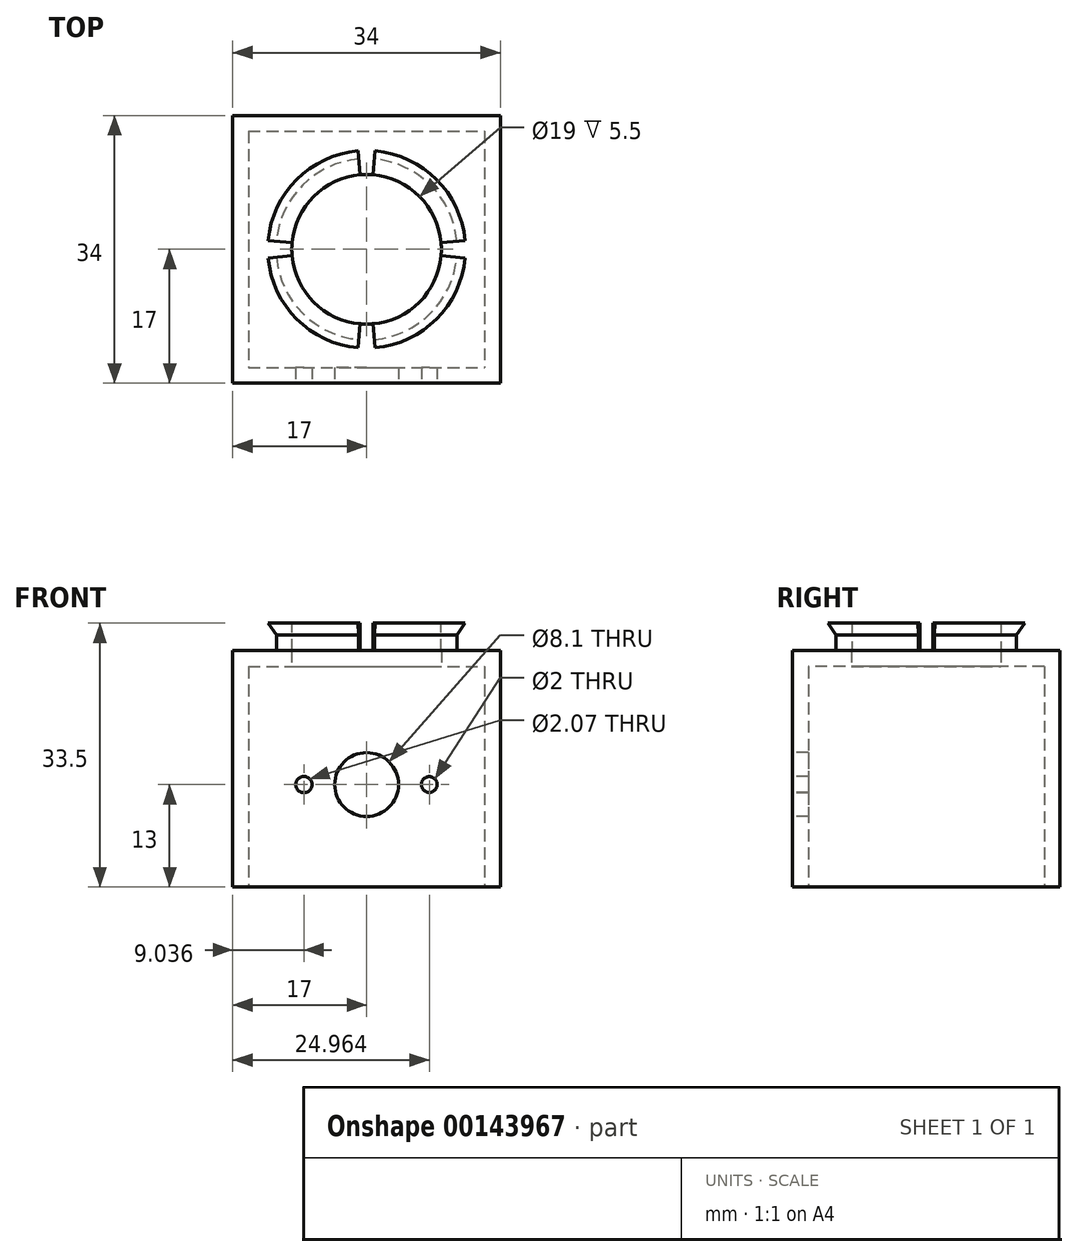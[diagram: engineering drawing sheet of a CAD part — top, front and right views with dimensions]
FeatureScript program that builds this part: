
annotation { "Feature Type Name" : "Feature", "Feature Type Description" : "" }
export const myFeature = defineFeature(function(context is Context, id is Id, definition is map)
    precondition{}
    {
        {
            var Q0;
            Q0=qCreatedBy(makeId("Top.planeOp"),FACE);
            var sketch = newSketch(context, id + "F0", { "sketchPlane" : qUnion([Q0])});
            skLineSegment(sketch, "E0.bottom", {"start": v(-15, 15) * mm, "end": v(15, 15) * mm});
            skLineSegment(sketch, "E0.top", {"start": v(-15, -15) * mm, "end": v(15, -15) * mm});
            skLineSegment(sketch, "E0.left", {"start": v(-15, 15) * mm, "end": v(-15, -15) * mm});
            skLineSegment(sketch, "E0.right", {"start": v(15, 15) * mm, "end": v(15, -15) * mm});
            skPoint(sketch, "E0.middle", {"position": v(0, 0) * mm});
            skLineSegment(sketch, "E1.bottom", {"start": v(0, 0) * mm, "end": v(0, 0) * mm});
            skLineSegment(sketch, "E1.top", {"start": v(0, 0) * mm, "end": v(0, 0) * mm});
            skLineSegment(sketch, "E1.left", {"start": v(0, 0) * mm, "end": v(0, 0) * mm});
            skLineSegment(sketch, "E1.right", {"start": v(0, 0) * mm, "end": v(0, 0) * mm});
            skLineSegment(sketch, "E2.bottom", {"start": v(-17, 17) * mm, "end": v(17, 17) * mm});
            skLineSegment(sketch, "E2.top", {"start": v(-17, -17) * mm, "end": v(17, -17) * mm});
            skLineSegment(sketch, "E2.left", {"start": v(-17, 17) * mm, "end": v(-17, -17) * mm});
            skLineSegment(sketch, "E2.right", {"start": v(17, 17) * mm, "end": v(17, -17) * mm});
            skSolve(sketch);
        }
        {
            var Q0;
            Q0=makeQuery(id+"F0.imprint","IMPRINT",FACE,{"disambiguationData":[TD([[makeQuery(id+"F0.imprint","IMPRINT",EDGE,{"derivedFrom":sQuery(id+"F0.wireOp",EDGE,"E0.bottom")}),1.0]])]});
            var Q1;
            Q1=makeQuery(id+"F0.imprint","IMPRINT",FACE,{"disambiguationData":[TD([[makeQuery(id+"F0.imprint","IMPRINT",EDGE,{"derivedFrom":sQuery(id+"F0.wireOp",EDGE,"E0.bottom")}),-1.0]])]});
            extrude(context, id + "F1", {"entities" : qUnion([Q0, Q1]), "oppositeDirection" : true, "depth" : 2 * mm});
        }
        {
            var Q0;
            Q0=makeQuery(id+"F0.imprint","IMPRINT",FACE,{"disambiguationData":[TD([[makeQuery(id+"F0.imprint","IMPRINT",EDGE,{"derivedFrom":sQuery(id+"F0.wireOp",EDGE,"E0.bottom")}),1.0]])]});
            extrude(context, id + "F2", {"entities" : qUnion([Q0]), "operationType" : NewBodyOperationType.ADD, "depth" : 28 * mm});
        }
        {
            var Q0;
            {var subQ0=sQuery(id+"F0.wireOp",EDGE,"E2.top");Q0=makeQuery(id+"F2.boolean.opBoolean","MERGE",FACE,{"derivedFrom":[makeQuery(id+"F1.opExtrude","SWEPT_FACE",FACE,{"disambiguationData":[OSD([subQ0])]}),makeQuery(id+"F2.opExtrude","SWEPT_FACE",FACE,{"disambiguationData":[OSD([subQ0])]})]});}
            var sketch = newSketch(context, id + "F3", { "sketchPlane" : qUnion([Q0])});
            skLineSegment(sketch, "E3.0", {"start": v(-17, -2) * mm, "end": v(17, -2) * mm});
            skLineSegment(sketch, "E4.0", {"start": v(-17, 28) * mm, "end": v(17, 28) * mm});
            skLineSegment(sketch, "E5", {"start": v(-17, -2) * mm, "end": v(17, 28) * mm, "construction": true});
            skPoint(sketch, "E6", {"position": v(0, 13) * mm});
            skCircle(sketch, "E7", {"center": v(0, 13) * mm, "radius": 4.05 * mm});
            skLineSegment(sketch, "E8.bottom", {"start": v(-9.96, 27.5) * mm, "end": v(9.96, 27.5) * mm, "construction": true});
            skLineSegment(sketch, "E8.top", {"start": v(-9.96, 3.5) * mm, "end": v(9.96, 3.5) * mm, "construction": true});
            skLineSegment(sketch, "E8.left", {"start": v(-9.96, 27.5) * mm, "end": v(-9.96, 3.5) * mm, "construction": true});
            skLineSegment(sketch, "E8.right", {"start": v(9.96, 27.5) * mm, "end": v(9.96, 3.5) * mm, "construction": true});
            skPoint(sketch, "E8.middle", {"position": v(0, 15.5) * mm});
            skLineSegment(sketch, "E9.bottom", {"start": v(-7.96, 25.5) * mm, "end": v(7.96, 25.5) * mm, "construction": true});
            skLineSegment(sketch, "E9.top", {"start": v(-7.96, 13) * mm, "end": v(7.96, 13) * mm, "construction": true});
            skLineSegment(sketch, "E9.left", {"start": v(-7.96, 25.5) * mm, "end": v(-7.96, 13) * mm, "construction": true});
            skLineSegment(sketch, "E9.right", {"start": v(7.96, 25.5) * mm, "end": v(7.96, 13) * mm, "construction": true});
            skCircle(sketch, "E10", {"center": v(7.96, 13) * mm, "radius": 1 * mm});
            skCircle(sketch, "E11", {"center": v(-7.96, 13) * mm, "radius": 1.04 * mm});
            skSolve(sketch);
        }
        {
            var Q0;
            Q0=makeQuery(id+"F2.opExtrude","CAP_FACE",FACE,{"disambiguationData":[OSD([sQuery(id+"F0.wireOp",EDGE,"E0.bottom"),sQuery(id+"F0.wireOp",EDGE,"E0.top"),sQuery(id+"F0.wireOp",EDGE,"E0.left"),sQuery(id+"F0.wireOp",EDGE,"E0.right"),sQuery(id+"F0.wireOp",EDGE,"E2.bottom"),sQuery(id+"F0.wireOp",EDGE,"E2.top"),sQuery(id+"F0.wireOp",EDGE,"E2.left"),sQuery(id+"F0.wireOp",EDGE,"E2.right")])],"isStart":false});
            var sketch = newSketch(context, id + "F4", { "sketchPlane" : qUnion([Q0])});
            skLineSegment(sketch, "E12.0", {"start": v(-17, 17) * mm, "end": v(17, 17) * mm});
            skLineSegment(sketch, "E13.0", {"start": v(-17, 17) * mm, "end": v(-17, -17) * mm});
            skLineSegment(sketch, "E14.0", {"start": v(-17, -17) * mm, "end": v(17, -17) * mm});
            skLineSegment(sketch, "E15.0", {"start": v(17, 17) * mm, "end": v(17, -17) * mm});
            skCircle(sketch, "E16", {"center": v(0, 0) * mm, "radius": 11.5 * mm});
            skCircle(sketch, "E17", {"center": v(0, 0) * mm, "radius": 10.5 * mm});
            skLineSegment(sketch, "E18", {"start": v(0, 0) * mm, "end": v(-11.46, 1) * mm});
            skLineSegment(sketch, "E19", {"start": v(0, 0) * mm, "end": v(-11.46, -1) * mm});
            skLineSegment(sketch, "E20", {"start": v(0, 0) * mm, "end": v(11.46, 1) * mm});
            skLineSegment(sketch, "E21", {"start": v(0, 0) * mm, "end": v(11.46, -1) * mm});
            skLineSegment(sketch, "E22", {"start": v(-11.5, 0) * mm, "end": v(11.5, 0) * mm, "construction": true});
            skSolve(sketch);
        }
        {
            var Q0;
            Q0=makeQuery(id+"F4.imprint","IMPRINT",FACE,{"disambiguationData":[TD([[makeQuery(id+"F4.imprint","IMPRINT",EDGE,{"derivedFrom":sQuery(id+"F4.wireOp",EDGE,"E12.0")}),-1.0]])]});
            var Q1;
            Q1=makeQuery(id+"F4.imprint","IMPRINT",FACE,{"disambiguationData":[TD([[makeQuery(id+"F4.imprint","IMPRINT",EDGE,{"derivedFrom":makeQuery(id+"F2.opExtrude","CAP_EDGE",EDGE,{"disambiguationData":[OSD([sQuery(id+"F0.wireOp",EDGE,"E0.bottom")])],"isStart":false})}),-1.0]])]});
            extrude(context, id + "F5", {"entities" : qUnion([Q0, Q1]), "operationType" : NewBodyOperationType.ADD, "depth" : 2 * mm});
        }
        {
            var Q0;
            Q0=qCreatedBy(makeId("Front.planeOp"),FACE);
            var sketch = newSketch(context, id + "F6", { "sketchPlane" : qUnion([Q0])});
            skLineSegment(sketch, "E23", {"start": v(0, 0) * mm, "end": v(0, 55.92) * mm, "construction": true});
            skLineSegment(sketch, "E24.0", {"start": v(-17, 30) * mm, "end": v(17, 30) * mm});
            skLineSegment(sketch, "E25", {"start": v(-11.5, 30) * mm, "end": v(-11.5, 32) * mm});
            skLineSegment(sketch, "E26", {"start": v(-11.5, 32) * mm, "end": v(-12.55, 33.5) * mm});
            skLineSegment(sketch, "E27", {"start": v(-12.55, 33.5) * mm, "end": v(0, 33.5) * mm});
            skLineSegment(sketch, "E28", {"start": v(-9.5, 30) * mm, "end": v(-9.5, 33.5) * mm});
            skLineSegment(sketch, "E29.0", {"start": v(-10.5, 28) * mm, "end": v(10.5, 28) * mm});
            skLineSegment(sketch, "E30", {"start": v(0, 28) * mm, "end": v(-17, 28) * mm, "construction": true});
            skLineSegment(sketch, "E31", {"start": v(-11.5, 30) * mm, "end": v(-11.5, 28) * mm});
            skLineSegment(sketch, "E32", {"start": v(-11.5, 28) * mm, "end": v(-9.5, 28) * mm});
            skLineSegment(sketch, "E33", {"start": v(-9.5, 28) * mm, "end": v(-9.5, 30) * mm});
            skSolve(sketch);
        }
        {
            var Q0;
            {var subQ3=sQuery(id+"F6.wireOp",EDGE,"E25");Q0=makeQuery(id+"F6.imprint","IMPRINT",FACE,{"disambiguationData":[TD([[makeQuery(id+"F6.imprint","IMPRINT",EDGE,{"derivedFrom":subQ3}),-1.0]])]});}
            var Q1;
            {var subQ0=sQuery(id+"F6.wireOp",EDGE,"E31");Q1=makeQuery(id+"F6.imprint","IMPRINT",FACE,{"disambiguationData":[TD([[makeQuery(id+"F6.imprint","IMPRINT",EDGE,{"derivedFrom":subQ0}),1.0]])]});}
            var Q2;
            Q2=sQuery(id+"F6.wireOp",EDGE,"E23");
            revolve(context, id + "F7", {"operationType" : NewBodyOperationType.ADD, "entities" : qUnion([Q0, Q1]), "axis" : qUnion([Q2]), "revolveType" : RevolveType.FULL});
        }
        {
            var Q0;
            Q0=makeQuery(id+"F7.opRevolve","SWEPT_FACE",FACE,{"disambiguationData":[OSD([sQuery(id+"F6.wireOp",EDGE,"E27")])]});
            var sketch = newSketch(context, id + "F8", { "sketchPlane" : qUnion([Q0])});
            skLineSegment(sketch, "E34.0", {"start": v(0, 0) * mm, "end": v(11.46, -1) * mm});
            skLineSegment(sketch, "E35.0", {"start": v(0, 0) * mm, "end": v(11.46, 1) * mm});
            skLineSegment(sketch, "E36.0", {"start": v(0, 0) * mm, "end": v(-11.46, -1) * mm});
            skLineSegment(sketch, "E37.0", {"start": v(0, 0) * mm, "end": v(-11.46, 1) * mm});
            skLineSegment(sketch, "E38", {"start": v(0, 0) * mm, "end": v(12.5, -1.1) * mm});
            skLineSegment(sketch, "E39", {"start": v(0, 0) * mm, "end": v(-12.5, -1.1) * mm});
            skLineSegment(sketch, "E40", {"start": v(0, 0) * mm, "end": v(-12.5, 1.1) * mm});
            skLineSegment(sketch, "E41", {"start": v(0, 0) * mm, "end": v(12.5, 1.1) * mm});
            skLineSegment(sketch, "E42", {"start": v(0, 0) * mm, "end": v(1.1, -12.5) * mm});
            skLineSegment(sketch, "E43", {"start": v(0, 0) * mm, "end": v(-1.1, -12.5) * mm});
            skLineSegment(sketch, "E44", {"start": v(0, 0) * mm, "end": v(-1.1, 12.5) * mm});
            skLineSegment(sketch, "E45", {"start": v(0, 0) * mm, "end": v(1.1, 12.5) * mm});
            skSolve(sketch);
        }
        {
            var Q0;
            {var subQ7=sQuery(id+"F8.wireOp",EDGE,"E38");var subQ8=makeQuery(id+"F8.imprint","IMPRINT",VERTEX,{"derivedFrom":subQ7});Q0=makeQuery(id+"F8.imprint","IMPRINT",FACE,{"disambiguationData":[TD([[makeQuery(id+"F8.imprint","IMPRINT",EDGE,{"disambiguationData":[TD([[subQ8,1.0]])],"derivedFrom":subQ7}),1.0]])]});}
            var Q1;
            {var subQ1=sQuery(id+"F8.wireOp",EDGE,"E38");var subQ3=makeQuery(id+"F7.opRevolve","SWEPT_EDGE",EDGE,{"disambiguationData":[OSD([sQuery(id+"F6.wireOp",EDGE,"E27"),sQuery(id+"F6.wireOp",EDGE,"E28")])]});var subQ4=makeQuery(id+"F8.imprint","INTERSECT",VERTEX,{"derivedFrom":[subQ3,subQ1]});Q1=makeQuery(id+"F8.imprint","IMPRINT",FACE,{"disambiguationData":[TD([[makeQuery(id+"F8.imprint","IMPRINT",EDGE,{"disambiguationData":[TD([[subQ4,1.0]])],"derivedFrom":subQ1}),1.0]])]});}
            var Q2;
            {var subQ1=sQuery(id+"F8.wireOp",EDGE,"E39");var subQ3=makeQuery(id+"F7.opRevolve","SWEPT_EDGE",EDGE,{"disambiguationData":[OSD([sQuery(id+"F6.wireOp",EDGE,"E27"),sQuery(id+"F6.wireOp",EDGE,"E28")])]});var subQ4=makeQuery(id+"F8.imprint","INTERSECT",VERTEX,{"derivedFrom":[subQ3,subQ1]});Q2=makeQuery(id+"F8.imprint","IMPRINT",FACE,{"disambiguationData":[TD([[makeQuery(id+"F8.imprint","IMPRINT",EDGE,{"disambiguationData":[TD([[subQ4,1.0]])],"derivedFrom":subQ1}),-1.0]])]});}
            var Q3;
            {var subQ7=sQuery(id+"F8.wireOp",EDGE,"E39");var subQ9=makeQuery(id+"F8.imprint","IMPRINT",VERTEX,{"derivedFrom":subQ7});Q3=makeQuery(id+"F8.imprint","IMPRINT",FACE,{"disambiguationData":[TD([[makeQuery(id+"F8.imprint","IMPRINT",EDGE,{"disambiguationData":[TD([[subQ9,1.0]])],"derivedFrom":subQ7}),-1.0]])]});}
            var Q4;
            {var subQ0=sQuery(id+"F8.wireOp",EDGE,"E42");var subQ1=sQuery(id+"F6.wireOp",EDGE,"E27");var subQ2=makeQuery(id+"F7.opRevolve","SWEPT_EDGE",EDGE,{"disambiguationData":[OSD([sQuery(id+"F6.wireOp",EDGE,"E26"),subQ1])]});var subQ3=makeQuery(id+"F8.imprint","INTERSECT",VERTEX,{"derivedFrom":[subQ2,subQ0]});Q4=makeQuery(id+"F8.imprint","IMPRINT",FACE,{"disambiguationData":[TD([[makeQuery(id+"F8.imprint","IMPRINT",EDGE,{"disambiguationData":[TD([[subQ3,1.0]])],"derivedFrom":subQ0}),-1.0]])]});}
            var Q5;
            {var subQ1=sQuery(id+"F8.wireOp",EDGE,"E42");var subQ3=makeQuery(id+"F7.opRevolve","SWEPT_EDGE",EDGE,{"disambiguationData":[OSD([sQuery(id+"F6.wireOp",EDGE,"E27"),sQuery(id+"F6.wireOp",EDGE,"E28")])]});var subQ4=makeQuery(id+"F8.imprint","INTERSECT",VERTEX,{"derivedFrom":[subQ3,subQ1]});Q5=makeQuery(id+"F8.imprint","IMPRINT",FACE,{"disambiguationData":[TD([[makeQuery(id+"F8.imprint","IMPRINT",EDGE,{"disambiguationData":[TD([[subQ4,-1.0]])],"derivedFrom":subQ3}),-1.0]])]});}
            var Q6;
            {var subQ1=sQuery(id+"F8.wireOp",EDGE,"E44");var subQ3=makeQuery(id+"F7.opRevolve","SWEPT_EDGE",EDGE,{"disambiguationData":[OSD([sQuery(id+"F6.wireOp",EDGE,"E27"),sQuery(id+"F6.wireOp",EDGE,"E28")])]});var subQ4=makeQuery(id+"F8.imprint","INTERSECT",VERTEX,{"derivedFrom":[subQ3,subQ1]});Q6=makeQuery(id+"F8.imprint","IMPRINT",FACE,{"disambiguationData":[TD([[makeQuery(id+"F8.imprint","IMPRINT",EDGE,{"disambiguationData":[TD([[subQ4,-1.0]])],"derivedFrom":subQ3}),-1.0]])]});}
            var Q7;
            {var subQ0=sQuery(id+"F8.wireOp",EDGE,"E44");var subQ1=sQuery(id+"F6.wireOp",EDGE,"E27");var subQ2=makeQuery(id+"F7.opRevolve","SWEPT_EDGE",EDGE,{"disambiguationData":[OSD([sQuery(id+"F6.wireOp",EDGE,"E26"),subQ1])]});var subQ3=makeQuery(id+"F8.imprint","INTERSECT",VERTEX,{"derivedFrom":[subQ2,subQ0]});Q7=makeQuery(id+"F8.imprint","IMPRINT",FACE,{"disambiguationData":[TD([[makeQuery(id+"F8.imprint","IMPRINT",EDGE,{"disambiguationData":[TD([[subQ3,1.0]])],"derivedFrom":subQ0}),-1.0]])]});}
            extrude(context, id + "F9", {"entities" : qUnion([Q0, Q1, Q2, Q3, Q4, Q5, Q6, Q7]), "operationType" : NewBodyOperationType.REMOVE, "oppositeDirection" : true, "depth" : 3.5 * mm});
        }
        {
            var Q0;
            Q0=makeQuery(id+"F3.imprint","IMPRINT",FACE,{"disambiguationData":[TD([[makeQuery(id+"F3.imprint","IMPRINT",EDGE,{"derivedFrom":sQuery(id+"F3.wireOp",EDGE,"E7")}),1.0]])]});
            var Q1;
            Q1=makeQuery(id+"F3.imprint","IMPRINT",FACE,{"disambiguationData":[TD([[makeQuery(id+"F3.imprint","IMPRINT",EDGE,{"derivedFrom":sQuery(id+"F3.wireOp",EDGE,"E10")}),1.0]])]});
            var Q2;
            Q2=makeQuery(id+"F3.imprint","IMPRINT",FACE,{"disambiguationData":[TD([[makeQuery(id+"F3.imprint","IMPRINT",EDGE,{"derivedFrom":sQuery(id+"F3.wireOp",EDGE,"E11")}),1.0]])]});
            extrude(context, id + "F10", {"entities" : qUnion([Q0, Q1, Q2]), "operationType" : NewBodyOperationType.REMOVE, "endBound" : BoundingType.UP_TO_NEXT, "oppositeDirection" : true, "depth" : 25 * mm});
        }
        {
            var Q0;
            Q0=makeQuery(id+"F1.opExtrude","CAP_FACE",FACE,{"disambiguationData":[OSD([sQuery(id+"F0.wireOp",EDGE,"E2.bottom"),sQuery(id+"F0.wireOp",EDGE,"E2.top"),sQuery(id+"F0.wireOp",EDGE,"E2.left"),sQuery(id+"F0.wireOp",EDGE,"E2.right")])],"isStart":false});
            var sketch = newSketch(context, id + "F11", { "sketchPlane" : qUnion([Q0])});
            skLineSegment(sketch, "E46.0", {"start": v(17, -17) * mm, "end": v(17, 17) * mm});
            skLineSegment(sketch, "E46.1", {"start": v(-17, 17) * mm, "end": v(17, 17) * mm});
            skLineSegment(sketch, "E46.2", {"start": v(-17, -17) * mm, "end": v(-17, 17) * mm});
            skLineSegment(sketch, "E46.3", {"start": v(-17, -17) * mm, "end": v(17, -17) * mm});
            skSolve(sketch);
        }
        {
            var Q0;
            Q0 = qSketchRegion(id + "F11", true);
            var Q1;
            Q1=makeQuery(id+"F11.imprint","IMPRINT",FACE,{"disambiguationData":[TD([[makeQuery(id+"F11.imprint","IMPRINT",EDGE,{"derivedFrom":sQuery(id+"F11.wireOp",EDGE,"E46.0")}),1.0]])]});
            extrude(context, id + "F12", {"entities" : qUnion([Q0, Q1]), "operationType" : NewBodyOperationType.REMOVE, "oppositeDirection" : true, "depth" : 2 * mm});
        }
    });
